# Revit family: PRD_FrankeWS_PrtctvSwtchs_CircuitBreaker_ZAQUA026
name_source: partatom
category: Electrical Fixtures
revit_build: Autodesk Revit 2018 (Build: 20190510_1515(x64)
units: mm (PartAtom-declared; Revit-internal decimal feet)

## family parameters
Always vertical = No
Cut with Voids When Loaded = No
Maintain Annotation Orientation = No
OmniClass Number = 23.80.40.14
OmniClass Title = Circuit Breakers
Part Type = Normal
Room Calculation Point = No
Round Connector Dimension = Use Diameter
Shared = No
Work Plane-Based = No

## types (1)
- ZAQUA026
    ApparentLoad = 0 VA
    AssetType = Fixed
    BIMObjectName = PRD_AR_ProtectiveSwitches_CircuitBreaker_ZAQUA026
    BodyMaterial = <By Category>
    Category = Pr_75_75_42_67, Protective switches
    Communication = No
    Current = 10 A
    Description = Power switch - A3000 open, for electronic module. Facilitates switching external loads, e.g. fans. With 2 switched outputs for controlling 2 separate devices, with maximum power rating 10 A - 230 V AC.
    DurationUnit = year
    Features = with 2 switched outputs for controlling 2 separate devices, with maximum power rating 10 A - 230 V AC
    GrossWeight = 0.30 kg
    HasProtectiveEarth = 0
    IfcExportAs = IfcDistributionElement
    IfcExportType = USERDEFINED
    InputSupplyVoltageV = 230.00 volt
    Manufacturer = KWC Group AG
    ManufacturerName = KWC Group AG
    ManufacturerURL = www.kwc.com
    Model = ZAQUA026
    ModelNumber = 2000101173
    ModelReference = ZAQUA026
    NBSDescription = Protective switches
    NBSReference = 90-75-40/370
    Name = Circuit breaker ZAQUA026
    NetWeight = 0.25 kg
    NominalDepth = 0 mm  [stored 0 ft]
    NominalFrequencyRange = 0 Hz
    NominalHeight = 0 mm  [stored 0 ft]
    NominalWidth = 0 mm  [stored 0 ft]
    NumberOfPoles = 0
    PowerFactor = 1
    PowerSwitch = Yes
    ProductInformation = https://pim.kwc.com
    RatedCurrent = 10 A
    RatedVoltage = 230 V
    URL = www.kwc.com
    Uniclass2015Code = Pr_75_75_42_67
    Uniclass2015Title = Protective switches
    Uniclass2015Version = Products v1.17
    Version = 1
    Voltage = 230 V
    WarrantyDurationUnit = year

note: [stored X ft] marks values corroborated as IEEE doubles in the binary element streams (Revit-internal decimal feet)

## geometry (parser evidence)
native form markers: Sweep x3
no freeform markers — native parametric forms only
